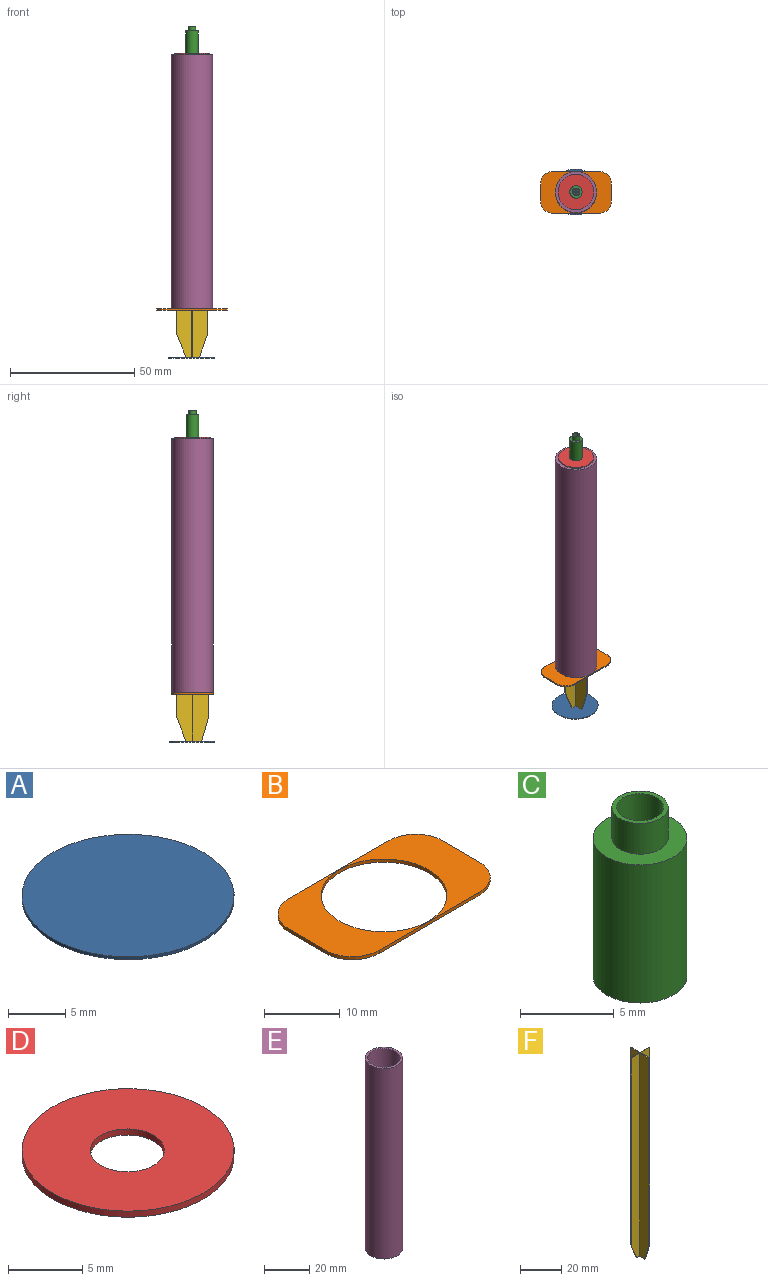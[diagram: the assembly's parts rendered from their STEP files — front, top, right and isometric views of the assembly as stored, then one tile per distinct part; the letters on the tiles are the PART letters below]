
ASSEMBLY  parts=6 mates=5
PART A: 3 faces, bbox 18.5x18.5x0.3 mm
  f0: cylinder r=9.25mm len=18.5mm, axis (0,0,-1), area 17.4mm2, adj f1,f2
  f1: plane 18.5x18.5mm, normal (0,0,1), area 268.8mm2, adj f0
  f2: plane 18.5x18.5mm, normal (0,0,-1), area 268.8mm2, adj f0
PART B: 11 faces, bbox 28.6x16.8x0.5 mm
  f0: plane 18.6x0.5mm, normal (0,1,0), area 9.3mm2, adj f5,f6,f9,f10
  f1: plane 6.8x0.5mm, normal (-1,0,0), area 3.4mm2, adj f5,f6,f7,f10
  f2: plane 18.6x0.5mm, normal (0,-1,0), area 9.3mm2, adj f5,f6,f7,f8
  f3: plane 6.8x0.5mm, normal (1,0,0), area 3.4mm2, adj f5,f6,f8,f9
  f4: cylinder r=8.3mm len=16.6mm, axis (0,0,1), area 26.1mm2, adj f5,f6
  f5: plane 28.6x16.8mm, normal (0,0,-1), area 242.6mm2, adj f0,f1,f2,f3,f4,f7,f8,f9
  f6: plane 28.6x16.8mm, normal (0,0,1), area 242.6mm2, adj f0,f1,f2,f3,f4,f7,f8,f9
  f7: cylinder r=5mm len=5mm, axis (0,0,1), area 3.9mm2, adj f1,f2,f5,f6
  f8: cylinder r=5mm len=5mm, axis (0,0,-1), area 3.9mm2, adj f2,f3,f5,f6
  f9: cylinder r=5mm len=5mm, axis (0,0,1), area 3.9mm2, adj f0,f3,f5,f6
  f10: cylinder r=5mm len=5mm, axis (0,0,-1), area 3.9mm2, adj f0,f1,f5,f6
PART C: 6 faces, bbox 5x5x11 mm
  f0: cylinder r=2.5mm len=9mm, axis (0,0,-1), area 141.4mm2, adj f1,f2
  f1: plane 5x5mm, normal (0,0,1), area 12.6mm2, adj f0,f3
  f2: plane 5x5mm, normal (0,0,-1), area 14.7mm2, adj f0,f4
  f3: cylinder r=1.5mm len=3mm, axis (0,0,-1), area 18.8mm2, adj f1,f5
  f4: cylinder r=1.25mm len=11mm, axis (0,0,-1), area 86.4mm2, adj f2,f5
  f5: plane 3x3mm, normal (0,0,1), area 2.2mm2, adj f3,f4
PART D: 4 faces, bbox 14.3x14.3x0.5 mm
  f0: cylinder r=2.5mm len=5mm, axis (0,0,1), area 7.9mm2, adj f2,f3
  f1: cylinder r=7.15mm len=14.3mm, axis (0,0,1), area 22.5mm2, adj f2,f3
  f2: plane 14.3x14.3mm, normal (0,0,-1), area 141mm2, adj f0,f1
  f3: plane 14.3x14.3mm, normal (0,0,1), area 141mm2, adj f0,f1
PART E: 4 faces, bbox 16.6x16.6x103 mm
  f0: cylinder r=7.15mm len=103mm, axis (0,0,-1), area 4627.3mm2, adj f2,f3
  f1: cylinder r=8.3mm len=103mm, axis (0,0,-1), area 5371.5mm2, adj f2,f3
  f2: plane 16.6x16.6mm, normal (0,0,-1), area 55.8mm2, adj f0,f1
  f3: plane 16.6x16.6mm, normal (0,0,1), area 55.8mm2, adj f0,f1
PART F: 18 faces, bbox 12.6x12.6x120 mm
  f0: plane 120x6.05mm, normal (1,0,0), area 709.3mm2, adj f2,f3,f4,f7,f17
  f1: plane 120x6.05mm, normal (-1,0,0), area 709.3mm2, adj f2,f3,f4,f7,f12
  f2: plane 9.5x3.58mm, normal (0,0.94,-0.35), area 5.1mm2, adj f0,f1,f3,f7
  f3: plane 110.51x0.5mm, normal (0,1,0), area 55.3mm2, adj f0,f1,f2,f4
  f4: plane 12.6x12.6mm, normal (0,0,1), area 9.9mm2, adj f0,f1,f3,f5,f8,f9,f10,f12
  f5: plane 110.68x0.5mm, normal (0,-1,0), area 55.3mm2, adj f4,f6,f8,f9
  f6: plane 9.32x2.73mm, normal (0,-0.96,-0.28), area 4.9mm2, adj f5,f7,f8,f9
  f7: plane 6.29x5.43mm, normal (0,0,-1), area 4.6mm2, adj f0,f1,f2,f6,f8,f9,f11,f12
  f8: plane 120x6.25mm, normal (1,0,0), area 737mm2, adj f4,f5,f6,f7,f16
  f9: plane 120x6.25mm, normal (-1,0,0), area 737mm2, adj f4,f5,f6,f7,f13
  f10: plane 110.42x0.3mm, normal (-1,0,0), area 33.1mm2, adj f4,f11,f12,f13
  f11: plane 9.58x3.81mm, normal (-0.93,0,-0.37), area 3.1mm2, adj f7,f10,f12,f13
  f12: plane 120x5.93mm, normal (0,1,0), area 693.6mm2, adj f1,f4,f7,f10,f11
  f13: plane 120x5.93mm, normal (0,-1,0), area 693.6mm2, adj f4,f7,f9,f10,f11
  f14: plane 9.58x3.37mm, normal (0.94,0,-0.33), area 3mm2, adj f7,f15,f16,f17
  f15: plane 110.42x0.3mm, normal (1,0,0), area 33.1mm2, adj f4,f14,f16,f17
  f16: plane 120x6.17mm, normal (0,-1,0), area 724.1mm2, adj f4,f7,f8,f14,f15
  f17: plane 120x6.17mm, normal (0,1,0), area 724.1mm2, adj f0,f4,f7,f14,f15
PLACE A t=(-0.29,0.05,-70.81)mm
PLACE B t=(0.01,-0.17,-51.01)mm
PLACE C t=(0,-0.17,51.99)mm
PLACE D t=(-0.07,-0.17,51.99)mm
PLACE E t=(0.01,-0.17,-51.51)mm fixed
PLACE F t=(-0.04,-0.1,-70.51)mm
MATE fastened B.f4 <-> E.f0  axis (0,0,-1) through (0.01,-0.17,-51.51)mm
MATE fastened E.f0 <-> D.f1  axis (0,0,1) through (0.01,-0.17,51.49)mm
MATE fastened D.f1 <-> C.f0  axis (0,0,1) through (0,-0.17,51.99)mm
MATE fastened F.f7 <-> A.f0  axis (0,0,-1) through (-0.29,0.05,-70.51)mm
MATE slider C.f0 <-> F.f4  axis (0,0,-1) through (0,-0.17,51.99)mm
